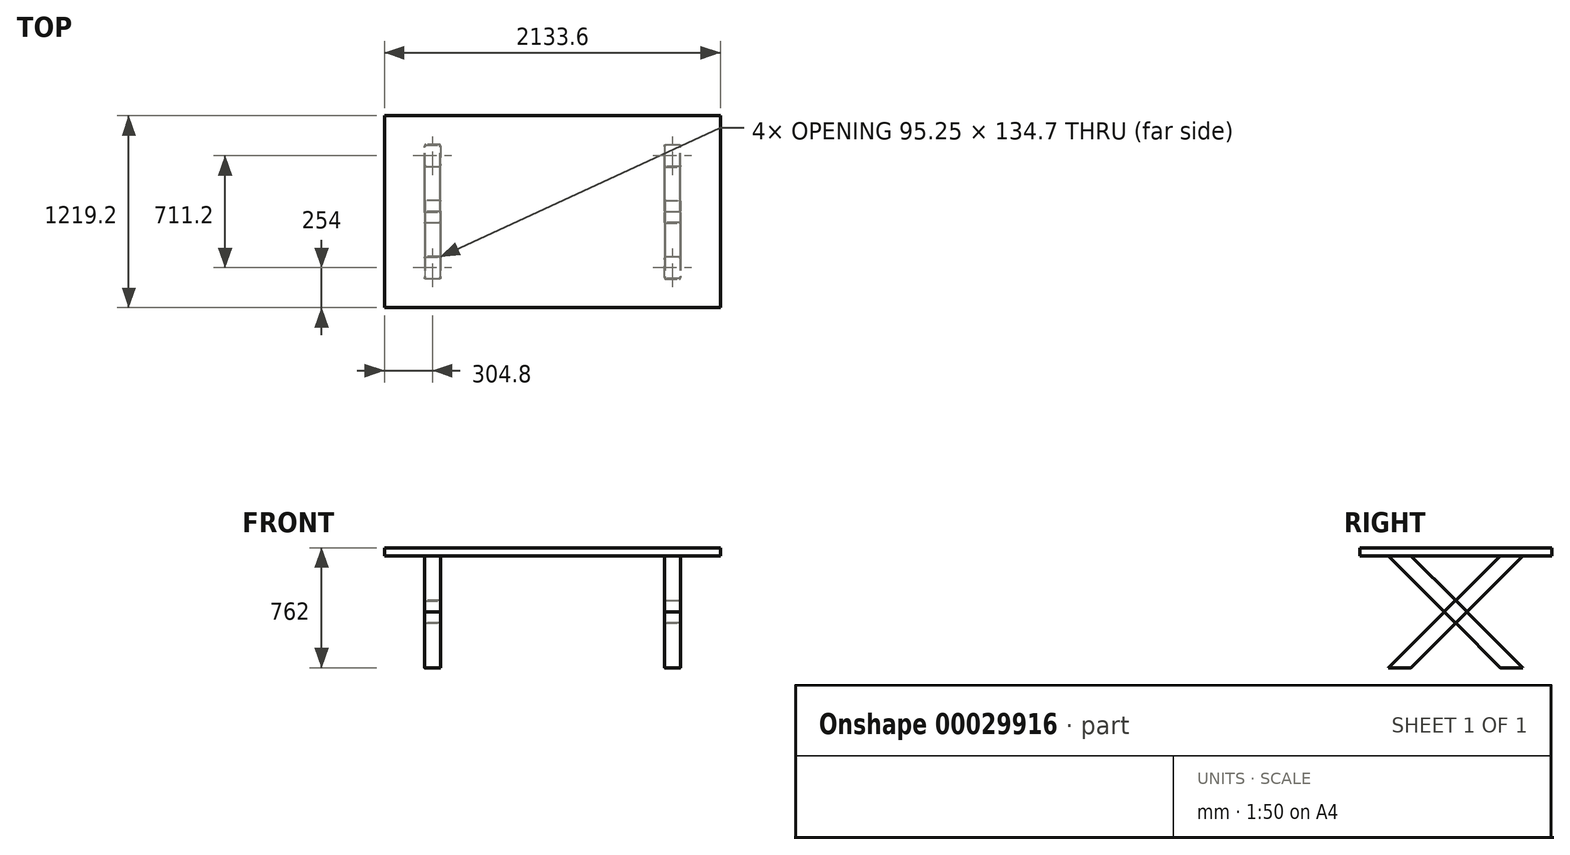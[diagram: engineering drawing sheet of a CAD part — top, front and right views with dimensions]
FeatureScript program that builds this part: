
annotation { "Feature Type Name" : "Feature", "Feature Type Description" : "" }
export const myFeature = defineFeature(function(context is Context, id is Id, definition is map)
    precondition{}
    {
        {
            var Q0;
            Q0=qCreatedBy(makeId("Front.planeOp"),FACE);
            var sketch = newSketch(context, id + "F12", { "sketchPlane" : qUnion([Q0])});
            skLineSegment(sketch, "E0.rect.bottom", {"start": v(1066.8, 25.4) * mm, "end": v(-1066.8, 25.4) * mm});
            skLineSegment(sketch, "E0.rect.top", {"start": v(1066.8, -25.4) * mm, "end": v(-1066.8, -25.4) * mm});
            skLineSegment(sketch, "E0.rect.left", {"start": v(1066.8, 25.4) * mm, "end": v(1066.8, -25.4) * mm});
            skLineSegment(sketch, "E0.rect.right", {"start": v(-1066.8, 25.4) * mm, "end": v(-1066.8, -25.4) * mm});
            skPoint(sketch, "E0.rect.middle", {"position": v(0, 0) * mm});
            skSolve(sketch);
        }
        {
            var Q0;
            Q0=makeQuery(id+"F12.imprint","IMPRINT",FACE,{"disambiguationData":[TD([[makeQuery(id+"F12.imprint","IMPRINT",EDGE,{"derivedFrom":sQuery(id+"F12.wireOp",EDGE,"E0.rect.bottom")}),1.0]])]});
            extrude(context, id + "F13", {"entities" : qUnion([Q0]), "endBound" : BoundingType.SYMMETRIC, "oppositeDirection" : true, "depth" : 1219.2 * mm});
        }
        {
            var Q0;
            Q0=makeQuery(id+"F13.opExtrude","SWEPT_FACE",FACE,{"disambiguationData":[OSD([sQuery(id+"F12.wireOp",EDGE,"E0.rect.left")])]});
            cPlane(context, id + "F0", {"entities" : qUnion([Q0]), "cplaneType" : CPlaneType.OFFSET, "offset" : 304.8 * mm, "oppositeDirection" : true, "width" : 152.4 * mm, "height" : 152.4 * mm});
        }
        {
            var Q0;
            Q0=qCreatedBy(id+"F0.planeOp",FACE);
            var sketch = newSketch(context, id + "F1", { "sketchPlane" : qUnion([Q0])});
            skLineSegment(sketch, "E1", {"start": v(-355.6, -25.4) * mm, "end": v(355.6, -736.6) * mm});
            skLineSegment(sketch, "E2", {"start": v(-355.6, -736.6) * mm, "end": v(355.6, -25.4) * mm});
            skPoint(sketch, "E3", {"position": v(0, -381) * mm});
            skSolve(sketch);
        }
        {
            var Q0;
            Q0=sQuery(id+"F1.wireOp",VERTEX,"E1.end");
            var Q1;
            Q1=sQuery(id+"F1.wireOp",EDGE,"E1");
            cPlane(context, id + "F2", {"entities" : qUnion([Q0, Q1]), "cplaneType" : CPlaneType.LINE_POINT, "offset" : 152.4 * mm, "width" : 152.4 * mm, "height" : 152.4 * mm});
        }
        {
            var Q0;
            Q0=qCreatedBy(id+"F2.planeOp",FACE);
            var sketch = newSketch(context, id + "F3", { "sketchPlane" : qUnion([Q0])});
            skLineSegment(sketch, "E4.rect.bottom", {"start": v(-717.55, -218.6) * mm, "end": v(-806.45, -218.6) * mm});
            skLineSegment(sketch, "E4.rect.top", {"start": v(-717.55, -320.2) * mm, "end": v(-806.45, -320.2) * mm});
            skLineSegment(sketch, "E4.rect.left", {"start": v(-711.2, -224.96) * mm, "end": v(-711.2, -313.86) * mm});
            skLineSegment(sketch, "E4.rect.right", {"start": v(-812.8, -224.96) * mm, "end": v(-812.8, -313.86) * mm});
            skPoint(sketch, "E4.rect.middle", {"position": v(-762, -269.4) * mm});
            skPoint(sketch, "E5.visualSharp", {"position": v(-812.8, -218.6) * mm});
            skArc(sketch, "E5.filletArc", {"start": v(-806.45, -218.6) * mm, "mid": v(-810.94, -220.47) * mm, "end": v(-812.8, -224.96) * mm});
            skPoint(sketch, "E6.visualSharp", {"position": v(-711.2, -218.6) * mm});
            skArc(sketch, "E6.filletArc", {"start": v(-711.2, -224.96) * mm, "mid": v(-713.06, -220.47) * mm, "end": v(-717.55, -218.6) * mm});
            skPoint(sketch, "E7.visualSharp", {"position": v(-711.2, -320.2) * mm});
            skArc(sketch, "E7.filletArc", {"start": v(-717.55, -320.2) * mm, "mid": v(-713.06, -318.35) * mm, "end": v(-711.2, -313.86) * mm});
            skPoint(sketch, "E8.visualSharp", {"position": v(-812.8, -320.2) * mm});
            skArc(sketch, "E8.filletArc", {"start": v(-812.8, -313.86) * mm, "mid": v(-810.94, -318.35) * mm, "end": v(-806.45, -320.2) * mm});
            skLineSegment(sketch, "E9.rect.bottom", {"start": v(-720.73, -221.78) * mm, "end": v(-803.28, -221.78) * mm});
            skLineSegment(sketch, "E9.rect.top", {"start": v(-720.73, -317.03) * mm, "end": v(-803.28, -317.03) * mm});
            skLineSegment(sketch, "E9.rect.left", {"start": v(-714.38, -228.13) * mm, "end": v(-714.38, -310.68) * mm});
            skLineSegment(sketch, "E9.rect.right", {"start": v(-809.63, -228.13) * mm, "end": v(-809.63, -310.68) * mm});
            skPoint(sketch, "E10.visualSharp", {"position": v(-809.63, -221.78) * mm});
            skArc(sketch, "E10.filletArc", {"start": v(-803.28, -221.78) * mm, "mid": v(-807.77, -223.64) * mm, "end": v(-809.63, -228.13) * mm});
            skPoint(sketch, "E11.visualSharp", {"position": v(-714.38, -221.78) * mm});
            skArc(sketch, "E11.filletArc", {"start": v(-714.38, -228.13) * mm, "mid": v(-716.23, -223.64) * mm, "end": v(-720.73, -221.78) * mm});
            skPoint(sketch, "E12.visualSharp", {"position": v(-714.38, -317.03) * mm});
            skArc(sketch, "E12.filletArc", {"start": v(-720.73, -317.03) * mm, "mid": v(-716.23, -315.17) * mm, "end": v(-714.38, -310.68) * mm});
            skPoint(sketch, "E13.visualSharp", {"position": v(-809.62, -317.03) * mm});
            skArc(sketch, "E13.filletArc", {"start": v(-809.63, -310.68) * mm, "mid": v(-807.77, -315.17) * mm, "end": v(-803.28, -317.03) * mm});
            skSolve(sketch);
        }
        {
            var Q0;
            Q0=makeQuery(id+"F3.imprint","IMPRINT",FACE,{"disambiguationData":[TD([[makeQuery(id+"F3.imprint","IMPRINT",EDGE,{"derivedFrom":sQuery(id+"F3.wireOp",EDGE,"E4.rect.bottom")}),1.0]])]});
            var Q1;
            Q1=makeQuery(id+"F13.opExtrude","SWEPT_FACE",FACE,{"disambiguationData":[OSD([sQuery(id+"F12.wireOp",EDGE,"E0.rect.top")])]});
            extrude(context, id + "F4", {"entities" : qUnion([Q0]), "endBound" : BoundingType.UP_TO_SURFACE, "oppositeDirection" : true, "endBoundEntityFace" : qUnion([Q1]), "depth" : 25.4 * mm});
        }
        {
            var Q0;
            Q0=makeQuery(id+"F4.opExtrude","CAP_FACE",FACE,{"disambiguationData":[OSD([sQuery(id+"F3.wireOp",EDGE,"E4.rect.bottom"),sQuery(id+"F3.wireOp",EDGE,"E4.rect.top"),sQuery(id+"F3.wireOp",EDGE,"E4.rect.left"),sQuery(id+"F3.wireOp",EDGE,"E4.rect.right"),sQuery(id+"F3.wireOp",EDGE,"E5.filletArc"),sQuery(id+"F3.wireOp",EDGE,"E6.filletArc"),sQuery(id+"F3.wireOp",EDGE,"E7.filletArc"),sQuery(id+"F3.wireOp",EDGE,"E8.filletArc"),sQuery(id+"F3.wireOp",EDGE,"E9.rect.bottom"),sQuery(id+"F3.wireOp",EDGE,"E9.rect.top"),sQuery(id+"F3.wireOp",EDGE,"E9.rect.left"),sQuery(id+"F3.wireOp",EDGE,"E9.rect.right"),sQuery(id+"F3.wireOp",EDGE,"E10.filletArc"),sQuery(id+"F3.wireOp",EDGE,"E11.filletArc"),sQuery(id+"F3.wireOp",EDGE,"E12.filletArc"),sQuery(id+"F3.wireOp",EDGE,"E13.filletArc")])],"isStart":true});
            extrude(context, id + "F5", {"entities" : qUnion([Q0]), "operationType" : NewBodyOperationType.ADD, "depth" : 239.6 * mm});
        }
        {
            var Q0;
            {var subQ0=sQuery(id+"F3.wireOp",EDGE,"E4.rect.right");Q0=makeQuery(id+"F5.boolean.opBoolean","MERGE",FACE,{"derivedFrom":[makeQuery(id+"F4.opExtrude","SWEPT_FACE",FACE,{"disambiguationData":[OSD([subQ0])]}),makeQuery(id+"F5.opExtrude","SWEPT_FACE",FACE,{"disambiguationData":[OSD([subQ0])]})]});}
            var sketch = newSketch(context, id + "F6", { "sketchPlane" : qUnion([Q0])});
            skLineSegment(sketch, "E14", {"start": v(283.76, -736.6) * mm, "end": v(427.44, -736.6) * mm});
            skLineSegment(sketch, "E15", {"start": v(427.44, -736.6) * mm, "end": v(560.94, -870.1) * mm});
            skLineSegment(sketch, "E16", {"start": v(560.94, -870.1) * mm, "end": v(489.1, -941.94) * mm});
            skLineSegment(sketch, "E17", {"start": v(489.1, -941.94) * mm, "end": v(283.76, -736.6) * mm});
            skSolve(sketch);
        }
        {
            var Q0;
            Q0 = qSketchRegion(id + "F6", true);
            var Q1;
            {var subQ0=sQuery(id+"F3.wireOp",EDGE,"E4.rect.left");Q1=makeQuery(id+"F5.boolean.opBoolean","MERGE",FACE,{"derivedFrom":[makeQuery(id+"F4.opExtrude","SWEPT_FACE",FACE,{"disambiguationData":[OSD([subQ0])]}),makeQuery(id+"F5.opExtrude","SWEPT_FACE",FACE,{"disambiguationData":[OSD([subQ0])]})]});}
            extrude(context, id + "F7", {"entities" : qUnion([Q0]), "operationType" : NewBodyOperationType.REMOVE, "endBound" : BoundingType.UP_TO_SURFACE, "oppositeDirection" : true, "endBoundEntityFace" : qUnion([Q1]), "depth" : 25.4 * mm});
        }
        {
            var Q0;
            Q0=makeQuery(id+"F4.opExtrude","SWEPT_BODY",BODY,{"disambiguationData":[OSD([sQuery(id+"F3.wireOp",EDGE,"E4.rect.bottom"),sQuery(id+"F3.wireOp",EDGE,"E4.rect.top"),sQuery(id+"F3.wireOp",EDGE,"E4.rect.left"),sQuery(id+"F3.wireOp",EDGE,"E4.rect.right"),sQuery(id+"F3.wireOp",EDGE,"E5.filletArc"),sQuery(id+"F3.wireOp",EDGE,"E6.filletArc"),sQuery(id+"F3.wireOp",EDGE,"E7.filletArc"),sQuery(id+"F3.wireOp",EDGE,"E8.filletArc"),sQuery(id+"F3.wireOp",EDGE,"E9.rect.bottom"),sQuery(id+"F3.wireOp",EDGE,"E9.rect.top"),sQuery(id+"F3.wireOp",EDGE,"E9.rect.left"),sQuery(id+"F3.wireOp",EDGE,"E9.rect.right"),sQuery(id+"F3.wireOp",EDGE,"E10.filletArc"),sQuery(id+"F3.wireOp",EDGE,"E11.filletArc"),sQuery(id+"F3.wireOp",EDGE,"E12.filletArc"),sQuery(id+"F3.wireOp",EDGE,"E13.filletArc")])]});
            var Q1;
            Q1=qCreatedBy(makeId("Front.planeOp"),FACE);
            mirror(context, id + "F8", {"entities" : qUnion([Q0]), "mirrorPlane" : qUnion([Q1])});
        }
        {
            var Q0;
            {var subQ0=sQuery(id+"F3.wireOp",EDGE,"E4.rect.right");Q0=makeQuery(id+"F5.boolean.opBoolean","MERGE",FACE,{"derivedFrom":[makeQuery(id+"F4.opExtrude","SWEPT_FACE",FACE,{"disambiguationData":[OSD([subQ0])]}),makeQuery(id+"F5.opExtrude","SWEPT_FACE",FACE,{"disambiguationData":[OSD([subQ0])]})]});}
            var sketch = newSketch(context, id + "F9", { "sketchPlane" : qUnion([Q0])});
            skLineSegment(sketch, "E18", {"start": v(0, -309.16) * mm, "end": v(71.84, -381) * mm});
            skLineSegment(sketch, "E19", {"start": v(71.84, -381) * mm, "end": v(0, -452.84) * mm});
            skLineSegment(sketch, "E20", {"start": v(0, -452.84) * mm, "end": v(-71.84, -381) * mm});
            skLineSegment(sketch, "E21", {"start": v(-71.84, -381) * mm, "end": v(0, -309.16) * mm});
            skSolve(sketch);
        }
        {
            var Q0;
            Q0 = qSketchRegion(id + "F9", true);
            var Q1;
            {var subQ0=sQuery(id+"F3.wireOp",EDGE,"E4.rect.left");Q1=makeQuery(id+"F5.boolean.opBoolean","MERGE",FACE,{"derivedFrom":[makeQuery(id+"F4.opExtrude","SWEPT_FACE",FACE,{"disambiguationData":[OSD([subQ0])]}),makeQuery(id+"F5.opExtrude","SWEPT_FACE",FACE,{"disambiguationData":[OSD([subQ0])]})]});}
            extrude(context, id + "F10", {"entities" : qUnion([Q0]), "operationType" : NewBodyOperationType.REMOVE, "endBound" : BoundingType.UP_TO_SURFACE, "oppositeDirection" : true, "endBoundEntityFace" : qUnion([Q1]), "depth" : 25.4 * mm});
        }
        {
            var Q0;
            Q0=makeQuery(id+"F4.opExtrude","SWEPT_BODY",BODY,{"disambiguationData":[OSD([sQuery(id+"F3.wireOp",EDGE,"E4.rect.bottom"),sQuery(id+"F3.wireOp",EDGE,"E4.rect.top"),sQuery(id+"F3.wireOp",EDGE,"E4.rect.left"),sQuery(id+"F3.wireOp",EDGE,"E4.rect.right"),sQuery(id+"F3.wireOp",EDGE,"E5.filletArc"),sQuery(id+"F3.wireOp",EDGE,"E6.filletArc"),sQuery(id+"F3.wireOp",EDGE,"E7.filletArc"),sQuery(id+"F3.wireOp",EDGE,"E8.filletArc"),sQuery(id+"F3.wireOp",EDGE,"E9.rect.bottom"),sQuery(id+"F3.wireOp",EDGE,"E9.rect.top"),sQuery(id+"F3.wireOp",EDGE,"E9.rect.left"),sQuery(id+"F3.wireOp",EDGE,"E9.rect.right"),sQuery(id+"F3.wireOp",EDGE,"E10.filletArc"),sQuery(id+"F3.wireOp",EDGE,"E11.filletArc"),sQuery(id+"F3.wireOp",EDGE,"E12.filletArc"),sQuery(id+"F3.wireOp",EDGE,"E13.filletArc")])]});
            var Q1;
            Q1=makeQuery(id+"F10.boolean.opBoolean","SPLIT",BODY,{"disambiguationData":[OD(1.0)],"derivedFrom":makeQuery(id+"F8.opPattern","COPY",BODY,{"derivedFrom":makeQuery(id+"F4.opExtrude","SWEPT_BODY",BODY,{"disambiguationData":[OSD([sQuery(id+"F3.wireOp",EDGE,"E4.rect.bottom"),sQuery(id+"F3.wireOp",EDGE,"E4.rect.top"),sQuery(id+"F3.wireOp",EDGE,"E4.rect.left"),sQuery(id+"F3.wireOp",EDGE,"E4.rect.right"),sQuery(id+"F3.wireOp",EDGE,"E5.filletArc"),sQuery(id+"F3.wireOp",EDGE,"E6.filletArc"),sQuery(id+"F3.wireOp",EDGE,"E7.filletArc"),sQuery(id+"F3.wireOp",EDGE,"E8.filletArc"),sQuery(id+"F3.wireOp",EDGE,"E9.rect.bottom"),sQuery(id+"F3.wireOp",EDGE,"E9.rect.top"),sQuery(id+"F3.wireOp",EDGE,"E9.rect.left"),sQuery(id+"F3.wireOp",EDGE,"E9.rect.right"),sQuery(id+"F3.wireOp",EDGE,"E10.filletArc"),sQuery(id+"F3.wireOp",EDGE,"E11.filletArc"),sQuery(id+"F3.wireOp",EDGE,"E12.filletArc"),sQuery(id+"F3.wireOp",EDGE,"E13.filletArc")])]}),"instanceName":"1"})});
            var Q2;
            Q2=makeQuery(id+"F10.boolean.opBoolean","SPLIT",BODY,{"disambiguationData":[OD(0.0)],"derivedFrom":makeQuery(id+"F8.opPattern","COPY",BODY,{"derivedFrom":makeQuery(id+"F4.opExtrude","SWEPT_BODY",BODY,{"disambiguationData":[OSD([sQuery(id+"F3.wireOp",EDGE,"E4.rect.bottom"),sQuery(id+"F3.wireOp",EDGE,"E4.rect.top"),sQuery(id+"F3.wireOp",EDGE,"E4.rect.left"),sQuery(id+"F3.wireOp",EDGE,"E4.rect.right"),sQuery(id+"F3.wireOp",EDGE,"E5.filletArc"),sQuery(id+"F3.wireOp",EDGE,"E6.filletArc"),sQuery(id+"F3.wireOp",EDGE,"E7.filletArc"),sQuery(id+"F3.wireOp",EDGE,"E8.filletArc"),sQuery(id+"F3.wireOp",EDGE,"E9.rect.bottom"),sQuery(id+"F3.wireOp",EDGE,"E9.rect.top"),sQuery(id+"F3.wireOp",EDGE,"E9.rect.left"),sQuery(id+"F3.wireOp",EDGE,"E9.rect.right"),sQuery(id+"F3.wireOp",EDGE,"E10.filletArc"),sQuery(id+"F3.wireOp",EDGE,"E11.filletArc"),sQuery(id+"F3.wireOp",EDGE,"E12.filletArc"),sQuery(id+"F3.wireOp",EDGE,"E13.filletArc")])]}),"instanceName":"1"})});
            var Q3;
            Q3=qCreatedBy(makeId("Right.planeOp"),FACE);
            mirror(context, id + "F11", {"entities" : qUnion([Q0, Q1, Q2]), "mirrorPlane" : qUnion([Q3])});
        }
    });
